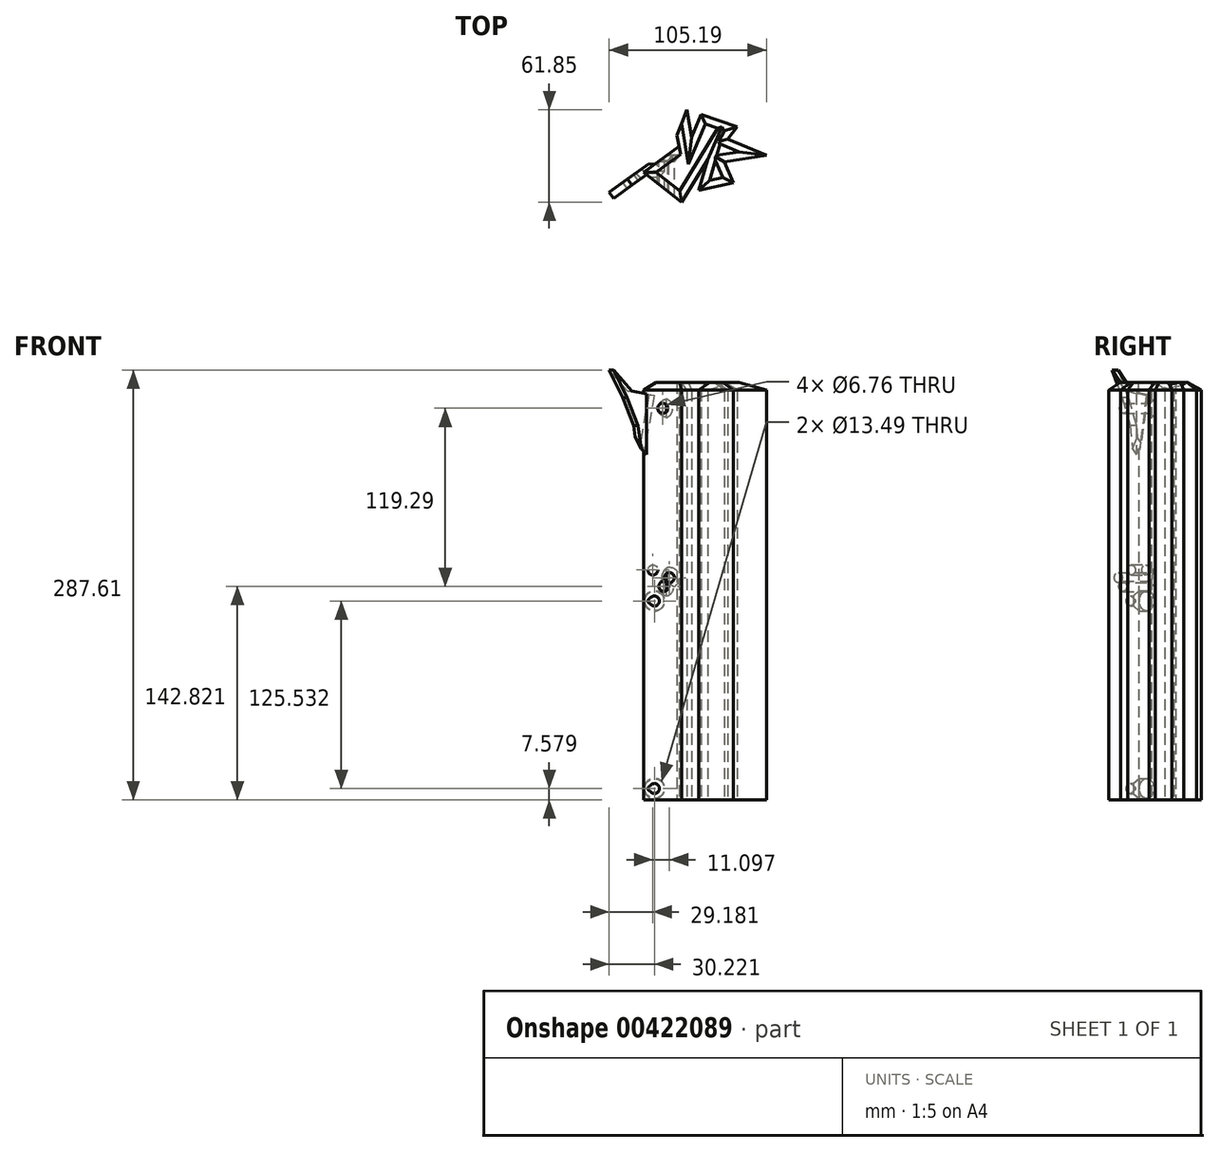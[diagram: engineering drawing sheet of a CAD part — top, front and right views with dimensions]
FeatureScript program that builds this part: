
annotation { "Feature Type Name" : "Feature", "Feature Type Description" : "" }
export const myFeature = defineFeature(function(context is Context, id is Id, definition is map)
    precondition{}
    {
        {
            var Q0;
            Q0=qCreatedBy(makeId("Top.planeOp"),FACE);
            var sketch = newSketch(context, id + "F0", { "sketchPlane" : qUnion([Q0])});
            skLineSegment(sketch, "E0", {"start": v(-23.83, 13.43) * mm, "end": v(-17.02, 30.64) * mm});
            skLineSegment(sketch, "E1", {"start": v(-17.02, 30.64) * mm, "end": v(-14, 12.3) * mm});
            skLineSegment(sketch, "E2", {"start": v(-14, 12.3) * mm, "end": v(-7.57, 27.43) * mm});
            skLineSegment(sketch, "E3", {"start": v(-7.57, 27.43) * mm, "end": v(16.46, 19.1) * mm});
            skLineSegment(sketch, "E4", {"start": v(16.46, 19.1) * mm, "end": v(10.21, 10.97) * mm});
            skLineSegment(sketch, "E5", {"start": v(10.21, 10.97) * mm, "end": v(36.13, 0) * mm});
            skLineSegment(sketch, "E6", {"start": v(36.13, 0) * mm, "end": v(7.94, -4.35) * mm});
            skLineSegment(sketch, "E7", {"start": v(7.94, -4.35) * mm, "end": v(14, -18.35) * mm});
            skLineSegment(sketch, "E8", {"start": v(14, -18.35) * mm, "end": v(-9.27, -23.27) * mm});
            skLineSegment(sketch, "E9", {"start": v(-9.27, -23.27) * mm, "end": v(-3.22, -2.65) * mm});
            skLineSegment(sketch, "E10", {"start": v(-3.22, -2.65) * mm, "end": v(-20.62, -31.2) * mm});
            skLineSegment(sketch, "E11", {"start": v(-20.62, -31.2) * mm, "end": v(-46.15, -11.16) * mm});
            skLineSegment(sketch, "E12", {"start": v(-46.15, -11.16) * mm, "end": v(-22.32, 6.24) * mm});
            skLineSegment(sketch, "E13", {"start": v(-22.32, 6.24) * mm, "end": v(-23.83, 13.43) * mm});
            skSolve(sketch);
        }
        {
            var Q0;
            Q0=makeQuery(id+"F0.imprint","IMPRINT",FACE,{"disambiguationData":[TD([[makeQuery(id+"F0.imprint","IMPRINT",EDGE,{"derivedFrom":sQuery(id+"F0.wireOp",EDGE,"E0")}),-1.0]])]});
            extrude(context, id + "F1", {"entities" : qUnion([Q0]), "endBound" : BoundingType.SYMMETRIC, "depth" : 279.4 * mm});
        }
        {
            var Q0;
            Q0=makeQuery(id+"F1.opExtrude","CAP_EDGE",EDGE,{"disambiguationData":[OSD([sQuery(id+"F0.wireOp",EDGE,"E8")])],"isStart":false});
            var Q1;
            Q1=makeQuery(id+"F1.opExtrude","CAP_EDGE",EDGE,{"disambiguationData":[OSD([sQuery(id+"F0.wireOp",EDGE,"E6")])],"isStart":false});
            var Q2;
            Q2=makeQuery(id+"F1.opExtrude","CAP_EDGE",EDGE,{"disambiguationData":[OSD([sQuery(id+"F0.wireOp",EDGE,"E4")])],"isStart":false});
            var Q3;
            Q3=makeQuery(id+"F1.opExtrude","CAP_EDGE",EDGE,{"disambiguationData":[OSD([sQuery(id+"F0.wireOp",EDGE,"E1")])],"isStart":false});
            var Q4;
            Q4=makeQuery(id+"F1.opExtrude","CAP_EDGE",EDGE,{"disambiguationData":[OSD([sQuery(id+"F0.wireOp",EDGE,"E10")])],"isStart":false});
            var Q5;
            Q5=makeQuery(id+"F1.opExtrude","CAP_EDGE",EDGE,{"disambiguationData":[OSD([sQuery(id+"F0.wireOp",EDGE,"E11")])],"isStart":false});
            var Q6;
            Q6=makeQuery(id+"F1.opExtrude","CAP_EDGE",EDGE,{"disambiguationData":[OSD([sQuery(id+"F0.wireOp",EDGE,"E12")])],"isStart":false});
            var Q7;
            Q7=makeQuery(id+"F1.opExtrude","CAP_EDGE",EDGE,{"disambiguationData":[OSD([sQuery(id+"F0.wireOp",EDGE,"E7")])],"isStart":false});
            var Q8;
            Q8=makeQuery(id+"F1.opExtrude","CAP_EDGE",EDGE,{"disambiguationData":[OSD([sQuery(id+"F0.wireOp",EDGE,"E2")])],"isStart":false});
            var Q9;
            Q9=makeQuery(id+"F1.opExtrude","CAP_EDGE",EDGE,{"disambiguationData":[OSD([sQuery(id+"F0.wireOp",EDGE,"E3")])],"isStart":false});
            var Q10;
            Q10=makeQuery(id+"F1.opExtrude","CAP_EDGE",EDGE,{"disambiguationData":[OSD([sQuery(id+"F0.wireOp",EDGE,"E5")])],"isStart":false});
            var Q11;
            Q11=makeQuery(id+"F1.opExtrude","CAP_EDGE",EDGE,{"disambiguationData":[OSD([sQuery(id+"F0.wireOp",EDGE,"E9")])],"isStart":false});
            chamfer(context, id + "F2", {"entities" : qUnion([Q0, Q1, Q2, Q3, Q4, Q5, Q6, Q7, Q8, Q9, Q10, Q11]), "width" : 5.08 * mm, "tangentPropagation" : true});
        }
        {
            var Q0;
            Q0=qCreatedBy(makeId("Front.planeOp"),FACE);
            var sketch = newSketch(context, id + "F3", { "sketchPlane" : qUnion([Q0])});
            skLineSegment(sketch, "E14", {"start": v(-33.3, 122.41) * mm, "end": v(-28.78, 9.02) * mm});
            skLineSegment(sketch, "E15", {"start": v(-28.78, 9.02) * mm, "end": v(-38.84, -132.12) * mm});
            skLineSegment(sketch, "E16", {"start": v(-38.84, -132.12) * mm, "end": v(-38.84, -6.59) * mm});
            skLineSegment(sketch, "E17", {"start": v(-38.84, -6.59) * mm, "end": v(-32.6, 3.12) * mm});
            skLineSegment(sketch, "E18", {"start": v(-32.6, 3.12) * mm, "end": v(-39.88, 14.22) * mm});
            skLineSegment(sketch, "E19", {"start": v(-39.88, 14.22) * mm, "end": v(-33.3, 122.41) * mm});
            skSolve(sketch);
        }
        {
            var Q0;
            Q0=sQuery(id+"F3.wireOp",VERTEX,"E14.start");
            var Q1;
            Q1=sQuery(id+"F3.wireOp",VERTEX,"E15.start");
            var Q2;
            Q2=sQuery(id+"F3.wireOp",VERTEX,"E19.start");
            var Q3;
            Q3=sQuery(id+"F3.wireOp",VERTEX,"E18.start");
            var Q4;
            Q4=sQuery(id+"F3.wireOp",VERTEX,"E17.start");
            var Q5;
            Q5=sQuery(id+"F3.wireOp",VERTEX,"E16.start");
            var Q6;
            Q6=makeQuery(id+"F1.opExtrude","SWEPT_BODY",BODY,{"disambiguationData":[OSD([sQuery(id+"F0.wireOp",EDGE,"E0"),sQuery(id+"F0.wireOp",EDGE,"E1"),sQuery(id+"F0.wireOp",EDGE,"E2"),sQuery(id+"F0.wireOp",EDGE,"E3"),sQuery(id+"F0.wireOp",EDGE,"E4"),sQuery(id+"F0.wireOp",EDGE,"E5"),sQuery(id+"F0.wireOp",EDGE,"E6"),sQuery(id+"F0.wireOp",EDGE,"E7"),sQuery(id+"F0.wireOp",EDGE,"E8"),sQuery(id+"F0.wireOp",EDGE,"E9"),sQuery(id+"F0.wireOp",EDGE,"E10"),sQuery(id+"F0.wireOp",EDGE,"E11"),sQuery(id+"F0.wireOp",EDGE,"E12"),sQuery(id+"F0.wireOp",EDGE,"E13")])]});
            hole(context, id + "F4", {"style" : HoleStyle.C_SINK, "endStyle" : HoleEndStyle.THROUGH, "oppositeDirection" : true, "holeDiameter" : 6.76 * mm, "cSinkDiameter" : 13.5 * mm, "cSinkAngle" : 82 * degree, "isTappedThrough" : true, "tappedDepth" : 12.7 * mm, "tapClearance" : 3, "locations" : qUnion([Q0, Q1, Q2, Q3, Q4, Q5]), "scope" : qUnion([Q6])});
        }
        {
            var Q0;
            Q0=makeQuery(id+"F1.opExtrude","SWEPT_FACE",FACE,{"disambiguationData":[OSD([sQuery(id+"F0.wireOp",EDGE,"E12")])]});
            var sketch = newSketch(context, id + "F5", { "sketchPlane" : qUnion([Q0])});
            skLineSegment(sketch, "E20", {"start": v(32.6, 130.57) * mm, "end": v(55.24, 133.92) * mm});
            skLineSegment(sketch, "E21", {"start": v(55.24, 133.92) * mm, "end": v(70.36, 147.91) * mm});
            skLineSegment(sketch, "E22", {"start": v(70.36, 147.91) * mm, "end": v(59.2, 129.38) * mm});
            skLineSegment(sketch, "E23", {"start": v(59.2, 129.38) * mm, "end": v(50.2, 110.87) * mm});
            skLineSegment(sketch, "E24", {"start": v(50.2, 110.87) * mm, "end": v(47.43, 95.15) * mm});
            skLineSegment(sketch, "E25", {"start": v(47.43, 95.15) * mm, "end": v(41.36, 89.84) * mm});
            skLineSegment(sketch, "E26", {"start": v(41.36, 89.84) * mm, "end": v(32.6, 130.57) * mm});
            skSolve(sketch);
        }
        {
            var Q0;
            Q0 = qSketchRegion(id + "F5", true);
            extrude(context, id + "F6", {"entities" : qUnion([Q0]), "operationType" : NewBodyOperationType.ADD, "endBound" : BoundingType.SYMMETRIC, "depth" : 5.08 * mm});
        }
        {
            var Q0;
            Q0=makeQuery(id+"F6.opExtrude","CAP_EDGE",EDGE,{"disambiguationData":[OSD([sQuery(id+"F5.wireOp",EDGE,"E25")])],"isStart":false});
            var Q1;
            Q1=makeQuery(id+"F6.opExtrude","CAP_EDGE",EDGE,{"disambiguationData":[OSD([sQuery(id+"F5.wireOp",EDGE,"E26")])],"isStart":false});
            chamfer(context, id + "F7", {"entities" : qUnion([Q0, Q1]), "width" : 5.08 * mm, "tangentPropagation" : true});
        }
    });
